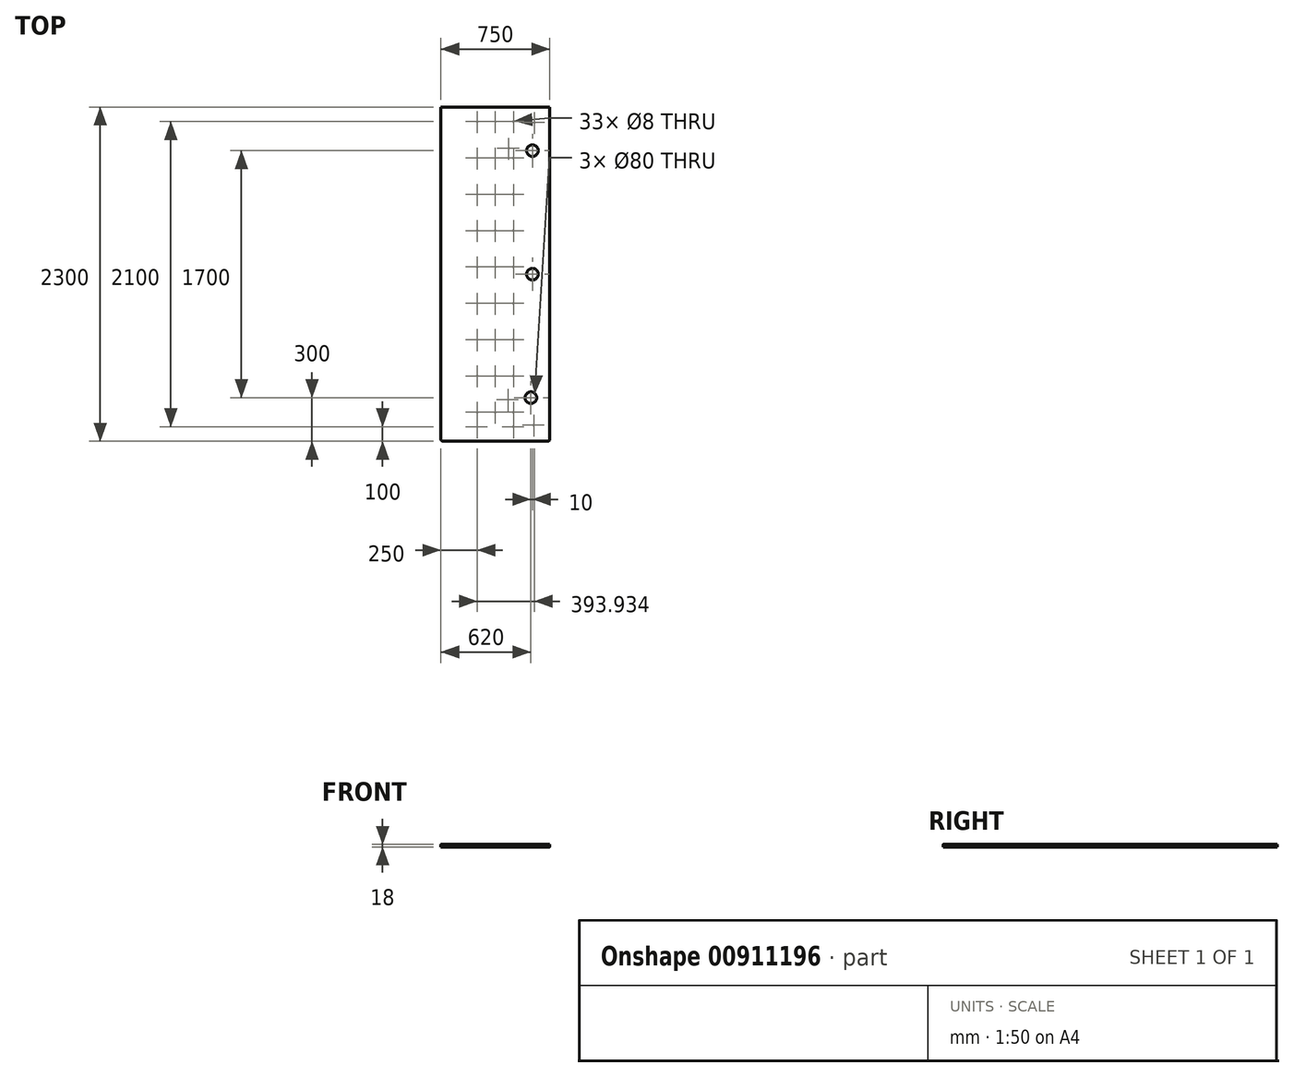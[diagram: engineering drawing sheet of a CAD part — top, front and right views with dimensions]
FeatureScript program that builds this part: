
annotation { "Feature Type Name" : "Feature", "Feature Type Description" : "" }
export const myFeature = defineFeature(function(context is Context, id is Id, definition is map)
    precondition{}
    {
        {
            var Q0;
            Q0=qCreatedBy(makeId("Top.planeOp"),FACE);
            var sketch = newSketch(context, id + "F0", { "sketchPlane" : qUnion([Q0])});
            skLineSegment(sketch, "E0", {"start": v(0, 0) * mm, "end": v(750, 0) * mm});
            skLineSegment(sketch, "E1", {"start": v(750, 0) * mm, "end": v(750, -2300) * mm});
            skLineSegment(sketch, "E2", {"start": v(750, -2300) * mm, "end": v(0, -2300) * mm});
            skLineSegment(sketch, "E3", {"start": v(0, -2300) * mm, "end": v(0, 0) * mm});
            skSolve(sketch);
        }
        {
            var Q0;
            Q0=makeQuery(id+"F0.imprint","IMPRINT",FACE,{"disambiguationData":[TD([[makeQuery(id+"F0.imprint","IMPRINT",EDGE,{"derivedFrom":sQuery(id+"F0.wireOp",EDGE,"E0")}),-1.0]])]});
            extrude(context, id + "F1", {"entities" : qUnion([Q0]), "depth" : 18 * mm, "offsetDistance" : 25 * mm});
        }
        {
            var Q0;
            Q0=makeQuery(id+"F1.opExtrude","SWEPT_EDGE",EDGE,{"disambiguationData":[OSD([sQuery(id+"F0.wireOp",EDGE,"E2"),sQuery(id+"F0.wireOp",EDGE,"E3")])]});
            var Q1;
            Q1=makeQuery(id+"F1.opExtrude","SWEPT_EDGE",EDGE,{"disambiguationData":[OSD([sQuery(id+"F0.wireOp",EDGE,"E1"),sQuery(id+"F0.wireOp",EDGE,"E2")])]});
            fillet(context, id + "F2", {"entities" : qUnion([Q0, Q1]), "radius" : 15 * mm, "tangentPropagation" : true, "allowEdgeOverflow" : false});
        }
        {
            var Q0;
            Q0=makeQuery(id+"F1.opExtrude","CAP_FACE",FACE,{"disambiguationData":[OSD([sQuery(id+"F0.wireOp",EDGE,"E0"),sQuery(id+"F0.wireOp",EDGE,"E1"),sQuery(id+"F0.wireOp",EDGE,"E2"),sQuery(id+"F0.wireOp",EDGE,"E3")])],"isStart":true});
            var sketch = newSketch(context, id + "F3", { "sketchPlane" : qUnion([Q0])});
            skCircle(sketch, "E4", {"center": v(250, 100) * mm, "radius": 4 * mm});
            skCircle(sketch, "E5", {"center": v(500, 100) * mm, "radius": 4 * mm});
            skLineSegment(sketch, "E6", {"start": v(500, 100) * mm, "end": v(375, 100) * mm});
            skLineSegment(sketch, "E7", {"start": v(375, 100) * mm, "end": v(250, 100) * mm});
            skLineSegment(sketch, "E8", {"start": v(500, 600) * mm, "end": v(500, 850) * mm});
            skLineSegment(sketch, "E9", {"start": v(500, 850) * mm, "end": v(500, 1100) * mm});
            skLineSegment(sketch, "E10", {"start": v(500, 1350) * mm, "end": v(500, 1600) * mm});
            skLineSegment(sketch, "E11", {"start": v(500, 1600) * mm, "end": v(500, 1850) * mm});
            skLineSegment(sketch, "E12", {"start": v(500, 1850) * mm, "end": v(500, 2100) * mm});
            skLineSegment(sketch, "E13", {"start": v(500, 2100) * mm, "end": v(500, 2200) * mm});
            skLineSegment(sketch, "E14", {"start": v(500, 2200) * mm, "end": v(250, 2200) * mm});
            skLineSegment(sketch, "E15", {"start": v(500, 2100) * mm, "end": v(250, 2100) * mm});
            skLineSegment(sketch, "E16", {"start": v(500, 1850) * mm, "end": v(250, 1850) * mm});
            skLineSegment(sketch, "E17", {"start": v(500, 1600) * mm, "end": v(250, 1600) * mm});
            skLineSegment(sketch, "E18", {"start": v(500, 1350) * mm, "end": v(250, 1350) * mm});
            skLineSegment(sketch, "E19", {"start": v(500, 1100) * mm, "end": v(250, 1100) * mm});
            skLineSegment(sketch, "E20", {"start": v(500, 850) * mm, "end": v(250, 850) * mm});
            skLineSegment(sketch, "E21", {"start": v(500, 600) * mm, "end": v(250, 600) * mm});
            skLineSegment(sketch, "E22", {"start": v(500, 350) * mm, "end": v(250, 350) * mm});
            skLineSegment(sketch, "E23", {"start": v(375, 100) * mm, "end": v(375, 350) * mm});
            skLineSegment(sketch, "E24", {"start": v(375, 350) * mm, "end": v(375, 600) * mm});
            skLineSegment(sketch, "E25", {"start": v(375, 600) * mm, "end": v(375, 850) * mm});
            skLineSegment(sketch, "E26", {"start": v(375, 850) * mm, "end": v(375, 1100) * mm});
            skLineSegment(sketch, "E27", {"start": v(375, 1100) * mm, "end": v(375, 1350) * mm});
            skLineSegment(sketch, "E28", {"start": v(375, 1350) * mm, "end": v(375, 1600) * mm});
            skLineSegment(sketch, "E29", {"start": v(375, 1600) * mm, "end": v(375, 1850) * mm});
            skLineSegment(sketch, "E30", {"start": v(375, 1850) * mm, "end": v(375, 2100) * mm});
            skLineSegment(sketch, "E31", {"start": v(750, 0) * mm, "end": v(643.93, 106.07) * mm});
            skCircle(sketch, "E32", {"center": v(643.93, 106.07) * mm, "radius": 4 * mm});
            skLineSegment(sketch, "E33", {"start": v(643.93, 106.07) * mm, "end": v(467.16, 282.84) * mm});
            skLineSegment(sketch, "E34", {"start": v(745.6, 2295.6) * mm, "end": v(639.54, 2189.54) * mm});
            skCircle(sketch, "E35", {"center": v(639.54, 2189.54) * mm, "radius": 4 * mm});
            skLineSegment(sketch, "E36", {"start": v(639.54, 2189.54) * mm, "end": v(462.76, 2012.76) * mm});
            skCircle(sketch, "E37", {"center": v(628.54, 1998.54) * mm, "radius": 40 * mm});
            skCircle(sketch, "E38", {"center": v(630, 310) * mm, "radius": 40 * mm});
            skSolve(sketch);
        }
        {
            var Q0;
            Q0=sQuery(id+"F3.wireOp",VERTEX,"E5.center");
            var Q1;
            Q1=sQuery(id+"F3.wireOp",VERTEX,"E4.center");
            var Q2;
            Q2=sQuery(id+"F3.wireOp",VERTEX,"E13.end");
            var Q3;
            Q3=sQuery(id+"F3.wireOp",VERTEX,"E12.end");
            var Q4;
            Q4=sQuery(id+"F3.wireOp",VERTEX,"E14.end");
            var Q5;
            Q5=sQuery(id+"F3.wireOp",VERTEX,"E15.end");
            var Q6;
            Q6=sQuery(id+"F3.wireOp",VERTEX,"E16.end");
            var Q7;
            Q7=sQuery(id+"F3.wireOp",VERTEX,"E11.end");
            var Q8;
            Q8=sQuery(id+"F3.wireOp",VERTEX,"E17.end");
            var Q9;
            Q9=sQuery(id+"F3.wireOp",VERTEX,"E10.end");
            var Q10;
            Q10=sQuery(id+"F3.wireOp",VERTEX,"E10.start");
            var Q11;
            Q11=sQuery(id+"F3.wireOp",VERTEX,"E18.end");
            var Q12;
            Q12=sQuery(id+"F3.wireOp",VERTEX,"E9.end");
            var Q13;
            Q13=sQuery(id+"F3.wireOp",VERTEX,"E19.end");
            var Q14;
            Q14=sQuery(id+"F3.wireOp",VERTEX,"E8.end");
            var Q15;
            Q15=sQuery(id+"F3.wireOp",VERTEX,"E20.end");
            var Q16;
            Q16=sQuery(id+"F3.wireOp",VERTEX,"E21.end");
            var Q17;
            Q17=sQuery(id+"F3.wireOp",VERTEX,"E8.start");
            var Q18;
            Q18=sQuery(id+"F3.wireOp",VERTEX,"E22.start");
            var Q19;
            Q19=sQuery(id+"F3.wireOp",VERTEX,"E22.end");
            var Q20;
            Q20=sQuery(id+"F3.wireOp",VERTEX,"E6.end");
            var Q21;
            Q21=sQuery(id+"F3.wireOp",VERTEX,"E23.end");
            var Q22;
            Q22=sQuery(id+"F3.wireOp",VERTEX,"E24.end");
            var Q23;
            Q23=sQuery(id+"F3.wireOp",VERTEX,"E25.end");
            var Q24;
            Q24=sQuery(id+"F3.wireOp",VERTEX,"E26.end");
            var Q25;
            Q25=sQuery(id+"F3.wireOp",VERTEX,"E27.end");
            var Q26;
            Q26=sQuery(id+"F3.wireOp",VERTEX,"E28.end");
            var Q27;
            Q27=sQuery(id+"F3.wireOp",VERTEX,"E29.end");
            var Q28;
            Q28=sQuery(id+"F3.wireOp",VERTEX,"E30.end");
            var Q29;
            Q29=sQuery(id+"F3.wireOp",VERTEX,"E31.end");
            var Q30;
            Q30=sQuery(id+"F3.wireOp",VERTEX,"E33.end");
            var Q31;
            Q31=sQuery(id+"F3.wireOp",VERTEX,"E34.end");
            var Q32;
            Q32=sQuery(id+"F3.wireOp",VERTEX,"E36.end");
            var Q33;
            Q33=makeQuery(id+"F1.opExtrude","SWEPT_BODY",BODY,{"disambiguationData":[OSD([sQuery(id+"F0.wireOp",EDGE,"E0"),sQuery(id+"F0.wireOp",EDGE,"E1"),sQuery(id+"F0.wireOp",EDGE,"E2"),sQuery(id+"F0.wireOp",EDGE,"E3")])]});
            hole(context, id + "F4", {"style" : HoleStyle.SIMPLE, "endStyle" : HoleEndStyle.BLIND, "holeDiameter" : 8 * mm, "majorDiameter" : 5 * mm, "holeDepth" : 15 * mm, "isTappedThrough" : true, "tappedDepth" : 12 * mm, "tapClearance" : 3, "locations" : qUnion([Q0, Q1, Q2, Q3, Q4, Q5, Q6, Q7, Q8, Q9, Q10, Q11, Q12, Q13, Q14, Q15, Q16, Q17, Q18, Q19, Q20, Q21, Q22, Q23, Q24, Q25, Q26, Q27, Q28, Q29, Q30, Q31, Q32]), "scope" : qUnion([Q33])});
        }
        {
            var Q0;
            Q0=makeQuery(id+"F1.opExtrude","CAP_FACE",FACE,{"disambiguationData":[OSD([sQuery(id+"F0.wireOp",EDGE,"E0"),sQuery(id+"F0.wireOp",EDGE,"E1"),sQuery(id+"F0.wireOp",EDGE,"E2"),sQuery(id+"F0.wireOp",EDGE,"E3")])],"isStart":true});
            var sketch = newSketch(context, id + "F5", { "sketchPlane" : qUnion([Q0])});
            skLineSegment(sketch, "E39", {"start": v(750, 0) * mm, "end": v(750, 300) * mm});
            skLineSegment(sketch, "E40", {"start": v(750, 300) * mm, "end": v(630, 300) * mm});
            skCircle(sketch, "E41", {"center": v(630, 300) * mm, "radius": 40 * mm});
            skLineSegment(sketch, "E42", {"start": v(735, 2300) * mm, "end": v(735, 2000) * mm});
            skLineSegment(sketch, "E43", {"start": v(735, 2000) * mm, "end": v(620, 2000) * mm});
            skCircle(sketch, "E44", {"center": v(620, 2000) * mm, "radius": 40 * mm});
            skCircle(sketch, "E45", {"center": v(630, 1150) * mm, "radius": 40 * mm});
            skSolve(sketch);
        }
        {
            var Q0;
            Q0 = qSketchRegion(id + "F5", true);
            extrude(context, id + "F6", {"entities" : qUnion([Q0]), "operationType" : NewBodyOperationType.REMOVE, "oppositeDirection" : true, "depth" : 18 * mm, "offsetDistance" : 25 * mm});
        }
    });
